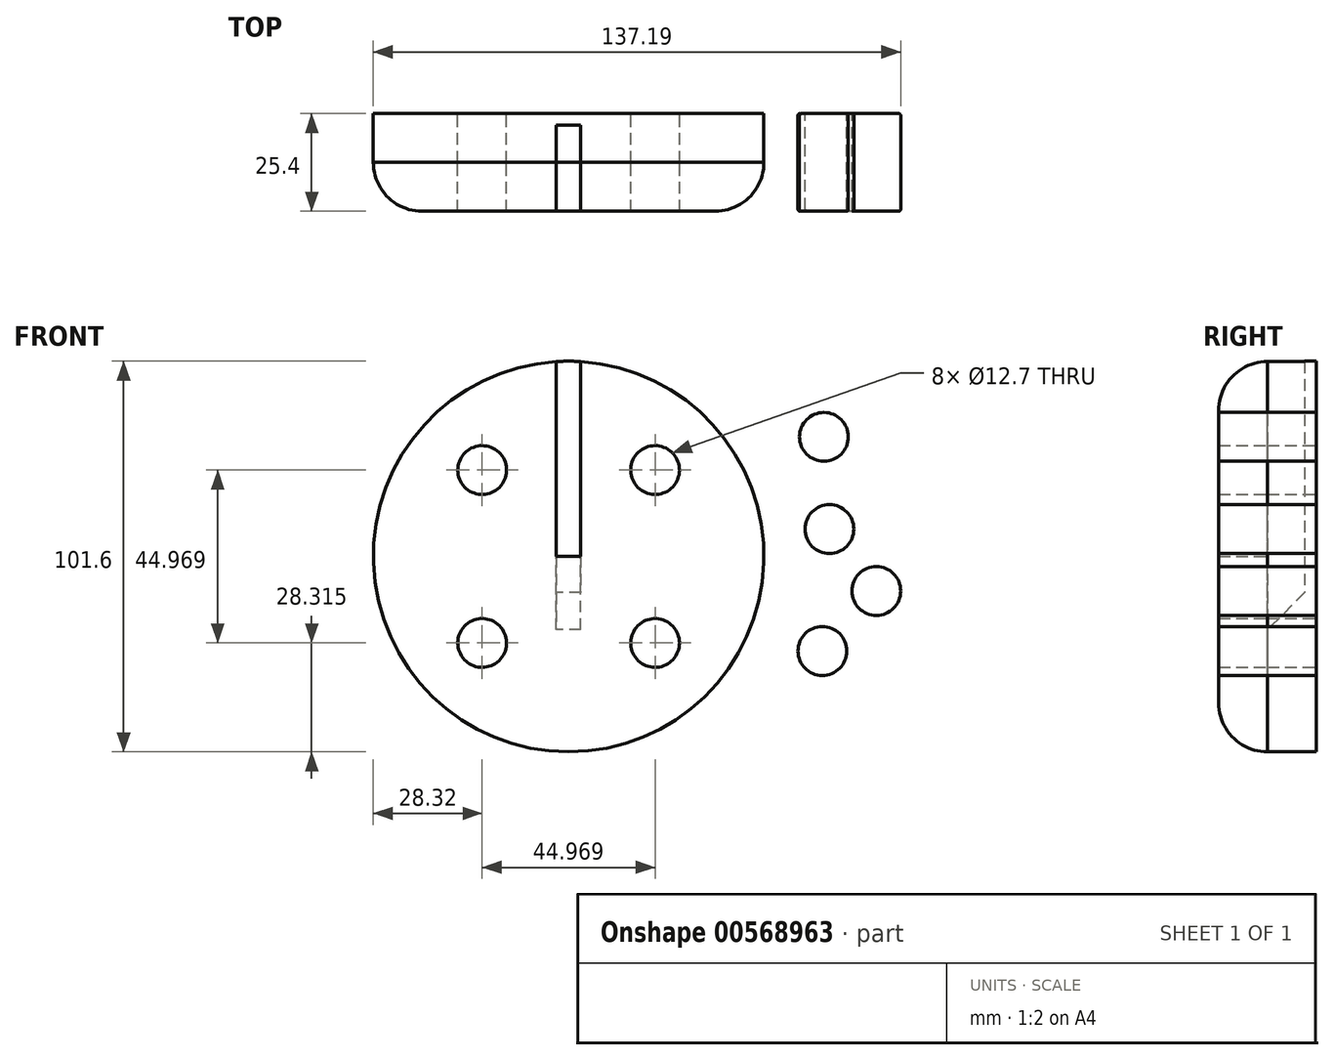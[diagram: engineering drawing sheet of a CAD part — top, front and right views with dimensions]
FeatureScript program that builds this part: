
annotation { "Feature Type Name" : "Feature", "Feature Type Description" : "" }
export const myFeature = defineFeature(function(context is Context, id is Id, definition is map)
    precondition{}
    {
        {
            var Q0;
            Q0=qCreatedBy(makeId("Front.planeOp"),FACE);
            var sketch = newSketch(context, id + "F0", { "sketchPlane" : qUnion([Q0])});
            skCircle(sketch, "E0", {"center": v(-11.18, 8.97) * mm, "radius": 50.8 * mm});
            skLineSegment(sketch, "E1.bottom", {"start": v(-14.35, 59.67) * mm, "end": v(-8, 59.67) * mm});
            skLineSegment(sketch, "E1.top", {"start": v(-14.35, 8.97) * mm, "end": v(-8, 8.97) * mm});
            skLineSegment(sketch, "E1.left", {"start": v(-14.35, 59.67) * mm, "end": v(-14.35, 8.97) * mm});
            skLineSegment(sketch, "E1.right", {"start": v(-8, 59.67) * mm, "end": v(-8, 8.97) * mm});
            skCircle(sketch, "E2", {"center": v(-33.66, 31.45) * mm, "radius": 6.35 * mm});
            skCircle(sketch, "E3", {"center": v(11.3, 31.45) * mm, "radius": 6.35 * mm});
            skCircle(sketch, "E4", {"center": v(-33.66, -13.51) * mm, "radius": 6.35 * mm});
            skCircle(sketch, "E5", {"center": v(11.3, -13.51) * mm, "radius": 6.35 * mm});
            skLineSegment(sketch, "E6", {"start": v(-33.66, 31.45) * mm, "end": v(11.3, -13.51) * mm, "construction": true});
            skLineSegment(sketch, "E7", {"start": v(-33.66, -13.51) * mm, "end": v(11.3, 31.45) * mm, "construction": true});
            skLineSegment(sketch, "E8.bottom", {"start": v(-33.66, 31.45) * mm, "end": v(11.3, 31.45) * mm, "construction": true});
            skLineSegment(sketch, "E8.top", {"start": v(-33.66, -13.51) * mm, "end": v(11.3, -13.51) * mm, "construction": true});
            skLineSegment(sketch, "E8.left", {"start": v(-33.66, 31.45) * mm, "end": v(-33.66, -13.51) * mm, "construction": true});
            skLineSegment(sketch, "E8.right", {"start": v(11.3, 31.45) * mm, "end": v(11.3, -13.51) * mm, "construction": true});
            skSolve(sketch);
        }
        {
            var Q0;
            Q0 = qSketchRegion(id + "F0", true);
            extrude(context, id + "F1", {"entities" : qUnion([Q0]), "depth" : 12.7 * mm, "offsetDistance" : 25.4 * mm});
        }
        {
            var Q0;
            Q0=makeQuery(id+"F1.opExtrude","CAP_FACE",FACE,{"disambiguationData":[OSD([sQuery(id+"F0.wireOp",EDGE,"E0")])],"isStart":false});
            extrude(context, id + "F2", {"entities" : qUnion([Q0]), "depth" : 12.7 * mm, "offsetDistance" : 25.4 * mm});
        }
        {
            var Q0;
            Q0=makeQuery(id+"F2.opExtrude","CAP_EDGE",EDGE,{"disambiguationData":[OSD([sQuery(id+"F0.wireOp",EDGE,"E0")])],"isStart":false});
            fillet(context, id + "F3", {"entities" : qUnion([Q0]), "radius" : 12.7 * mm, "tangentPropagation" : true, "allowEdgeOverflow" : false});
        }
        {
            var Q0;
            {var subQ0=sQuery(id+"F0.wireOp",EDGE,"E1.bottom");Q0=makeQuery(id+"F0.imprint","IMPRINT",FACE,{"disambiguationData":[TD([[makeQuery(id+"F0.imprint","IMPRINT",EDGE,{"derivedFrom":subQ0}),1.0]])]});}
            var Q1;
            Q1=makeQuery(id+"F0.imprint","IMPRINT",FACE,{"disambiguationData":[TD([[makeQuery(id+"F0.imprint","IMPRINT",EDGE,{"derivedFrom":sQuery(id+"F0.wireOp",EDGE,"E1.bottom")}),-1.0]])]});
            extrude(context, id + "F4", {"entities" : qUnion([Q0, Q1]), "operationType" : NewBodyOperationType.REMOVE, "depth" : 25.4 * mm, "offsetDistance" : 25.4 * mm, "hasSecondDirection" : true, "secondDirectionOppositeDirection" : false, "secondDirectionDepth" : 3.05 * mm});
        }
        {
            var Q0;
            Q0=makeQuery(id+"F4.boolean.opBoolean","INTERSECT",EDGE,{"derivedFrom":[makeQuery(id+"F1.opExtrude","CAP_FACE",FACE,{"disambiguationData":[OSD([sQuery(id+"F0.wireOp",EDGE,"E0")])],"isStart":false}),makeQuery(id+"F4.opExtrude","SWEPT_FACE",FACE,{"disambiguationData":[OSD([sQuery(id+"F0.wireOp",EDGE,"E1.top")])]})]});
            chamfer(context, id + "F5", {"entities" : qUnion([Q0]), "width" : 19.05 * mm, "tangentPropagation" : true});
        }
        {
            var Q0;
            Q0=qCreatedBy(makeId("Front.planeOp"),FACE);
            var sketch = newSketch(context, id + "F6", { "sketchPlane" : qUnion([Q0])});
            skCircle(sketch, "E9", {"center": v(55.24, 40.08) * mm, "radius": 6.35 * mm});
            skCircle(sketch, "E10", {"center": v(56.67, 16.1) * mm, "radius": 6.35 * mm});
            skCircle(sketch, "E11", {"center": v(54.84, -15.6) * mm, "radius": 6.35 * mm});
            skCircle(sketch, "E12", {"center": v(68.86, 0) * mm, "radius": 6.35 * mm});
            skSolve(sketch);
        }
        {
            var Q0;
            Q0 = qSketchRegion(id + "F6", true);
            extrude(context, id + "F7", {"entities" : qUnion([Q0]), "depth" : 25.4 * mm, "offsetDistance" : 25.4 * mm});
        }
        {
            var Q0;
            Q0=makeQuery(id+"F7.opExtrude","CAP_EDGE",EDGE,{"disambiguationData":[OSD([sQuery(id+"F6.wireOp",EDGE,"E9")])],"isStart":false});
            var Q1;
            Q1=makeQuery(id+"F7.opExtrude","CAP_EDGE",EDGE,{"disambiguationData":[OSD([sQuery(id+"F6.wireOp",EDGE,"E10")])],"isStart":false});
            var Q2;
            Q2=makeQuery(id+"F7.opExtrude","CAP_EDGE",EDGE,{"disambiguationData":[OSD([sQuery(id+"F6.wireOp",EDGE,"E10")])],"isStart":true});
            var Q3;
            Q3=makeQuery(id+"F7.opExtrude","CAP_EDGE",EDGE,{"disambiguationData":[OSD([sQuery(id+"F6.wireOp",EDGE,"E9")])],"isStart":true});
            var Q4;
            Q4=makeQuery(id+"F7.opExtrude","CAP_EDGE",EDGE,{"disambiguationData":[OSD([sQuery(id+"F6.wireOp",EDGE,"E12")])],"isStart":false});
            var Q5;
            Q5=makeQuery(id+"F7.opExtrude","CAP_EDGE",EDGE,{"disambiguationData":[OSD([sQuery(id+"F6.wireOp",EDGE,"E12")])],"isStart":true});
            var Q6;
            Q6=makeQuery(id+"F7.opExtrude","CAP_EDGE",EDGE,{"disambiguationData":[OSD([sQuery(id+"F6.wireOp",EDGE,"E11")])],"isStart":true});
            var Q7;
            Q7=makeQuery(id+"F7.opExtrude","CAP_EDGE",EDGE,{"disambiguationData":[OSD([sQuery(id+"F6.wireOp",EDGE,"E11")])],"isStart":false});
            fillet(context, id + "F8", {"entities" : qUnion([Q0, Q1, Q2, Q3, Q4, Q5, Q6, Q7]), "radius" : 0.5 * mm, "tangentPropagation" : true, "allowEdgeOverflow" : false});
        }
    });
